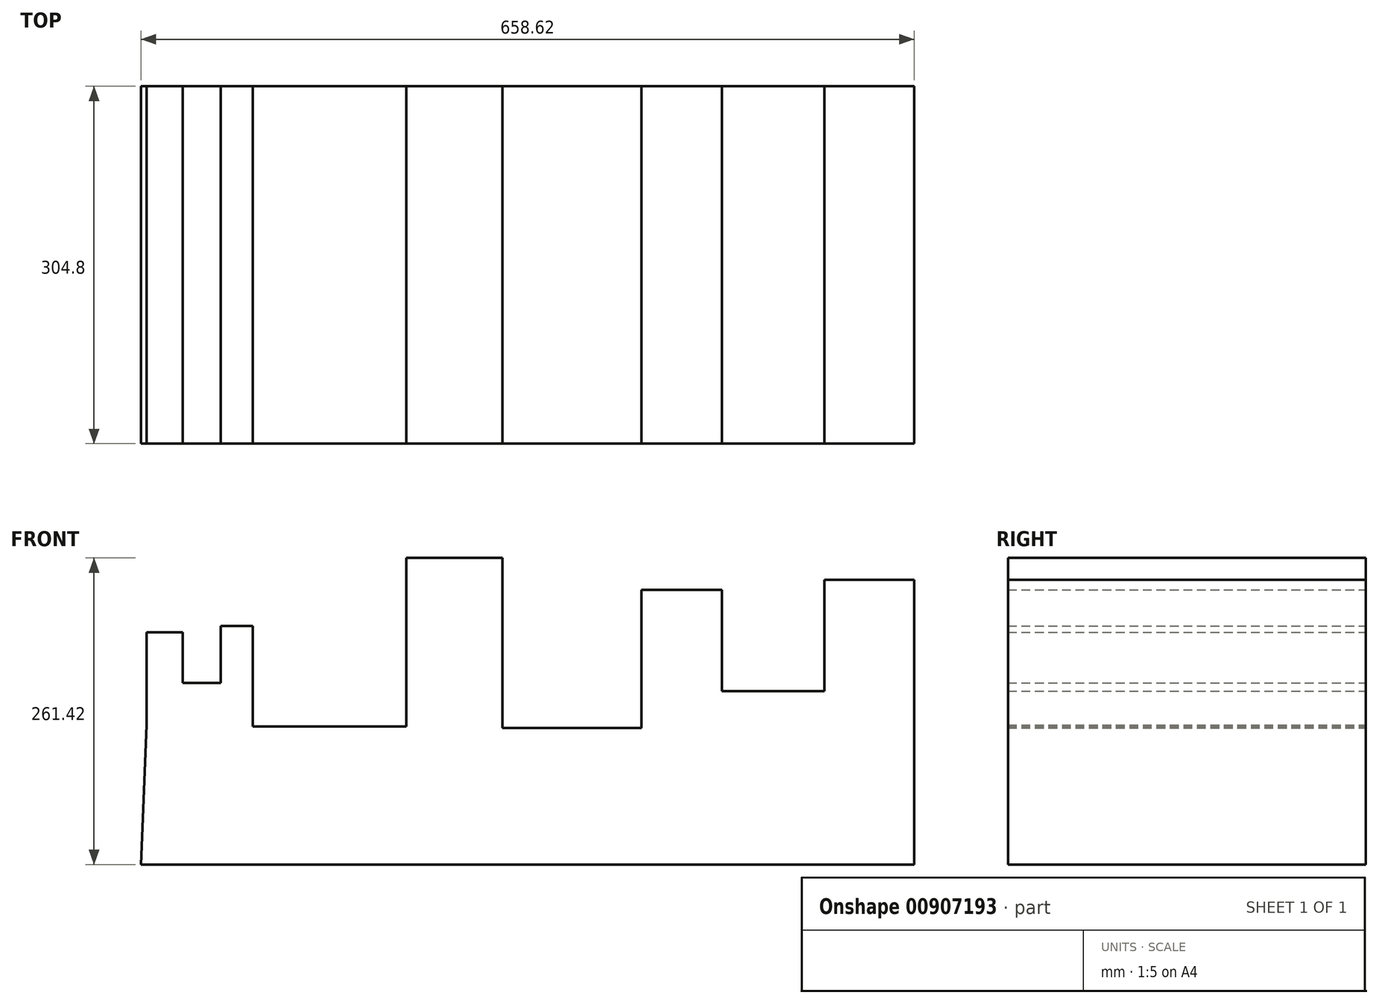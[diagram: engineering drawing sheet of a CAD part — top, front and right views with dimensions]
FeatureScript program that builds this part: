
annotation { "Feature Type Name" : "Feature", "Feature Type Description" : "" }
export const myFeature = defineFeature(function(context is Context, id is Id, definition is map)
    precondition{}
    {
        {
            var Q0;
            Q0=qCreatedBy(makeId("Front.planeOp"),FACE);
            var sketch = newSketch(context, id + "F0", { "sketchPlane" : qUnion([Q0])});
            skLineSegment(sketch, "E0", {"start": v(-30.72, 70.5) * mm, "end": v(-30.72, 149.38) * mm});
            skLineSegment(sketch, "E1", {"start": v(-30.72, 149.38) * mm, "end": v(0, 149.38) * mm});
            skLineSegment(sketch, "E2", {"start": v(0, 149.38) * mm, "end": v(0, 106.08) * mm});
            skLineSegment(sketch, "E3", {"start": v(0, 106.08) * mm, "end": v(32.43, 106.08) * mm});
            skLineSegment(sketch, "E4", {"start": v(32.43, 106.08) * mm, "end": v(32.43, 154.7) * mm});
            skLineSegment(sketch, "E5", {"start": v(32.43, 154.7) * mm, "end": v(59.74, 154.7) * mm});
            skLineSegment(sketch, "E6", {"start": v(59.74, 154.7) * mm, "end": v(59.74, 69.24) * mm});
            skLineSegment(sketch, "E7", {"start": v(59.74, 69.24) * mm, "end": v(190.58, 69.24) * mm});
            skLineSegment(sketch, "E8", {"start": v(190.58, 69.24) * mm, "end": v(190.58, 212.84) * mm});
            skLineSegment(sketch, "E9", {"start": v(190.58, 212.84) * mm, "end": v(272.61, 212.84) * mm});
            skLineSegment(sketch, "E10", {"start": v(272.61, 212.84) * mm, "end": v(272.61, 67.75) * mm});
            skLineSegment(sketch, "E11", {"start": v(272.61, 67.75) * mm, "end": v(390.92, 67.75) * mm});
            skLineSegment(sketch, "E12", {"start": v(390.92, 67.75) * mm, "end": v(390.92, 185.58) * mm});
            skLineSegment(sketch, "E13", {"start": v(390.92, 185.58) * mm, "end": v(459.56, 185.58) * mm});
            skLineSegment(sketch, "E14", {"start": v(459.56, 185.58) * mm, "end": v(459.56, 99.38) * mm});
            skLineSegment(sketch, "E15", {"start": v(459.56, 99.38) * mm, "end": v(546.84, 99.38) * mm});
            skLineSegment(sketch, "E16", {"start": v(546.84, 99.38) * mm, "end": v(546.84, 194.2) * mm});
            skLineSegment(sketch, "E17", {"start": v(546.84, 194.2) * mm, "end": v(623.27, 194.2) * mm});
            skLineSegment(sketch, "E18", {"start": v(623.27, 194.2) * mm, "end": v(623.27, -48.58) * mm});
            skLineSegment(sketch, "E19", {"start": v(623.27, -48.58) * mm, "end": v(-35.35, -48.58) * mm});
            skLineSegment(sketch, "E20", {"start": v(-35.35, -48.58) * mm, "end": v(-30.72, 70.5) * mm});
            skSolve(sketch);
        }
        {
            var Q0;
            Q0=makeQuery(id+"F0.imprint","IMPRINT",FACE,{"disambiguationData":[TD([[makeQuery(id+"F0.imprint","IMPRINT",EDGE,{"derivedFrom":sQuery(id+"F0.wireOp",EDGE,"E0")}),-1.0]])]});
            extrude(context, id + "F1", {"entities" : qUnion([Q0]), "depth" : 304.8 * mm, "offsetDistance" : 25.4 * mm});
        }
    });
